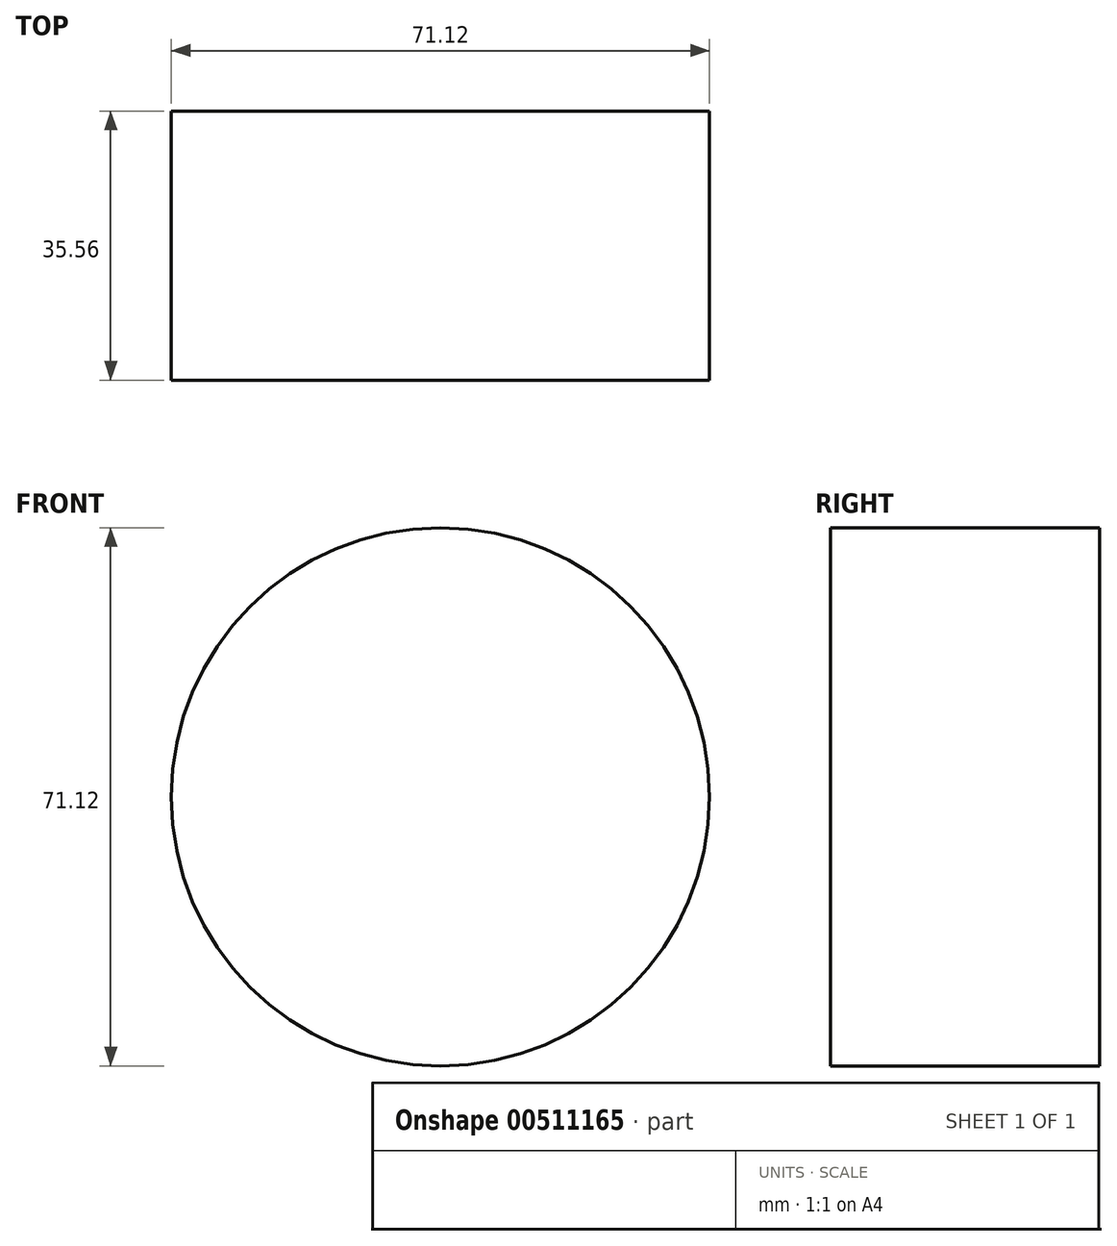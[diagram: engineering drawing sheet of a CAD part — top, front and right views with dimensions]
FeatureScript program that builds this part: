
annotation { "Feature Type Name" : "Feature", "Feature Type Description" : "" }
export const myFeature = defineFeature(function(context is Context, id is Id, definition is map)
    precondition{}
    {
        {
            var Q0;
            Q0=qCreatedBy(makeId("Top.planeOp"),FACE);
            var sketch = newSketch(context, id + "F0", { "sketchPlane" : qUnion([Q0])});
            skLineSegment(sketch, "E0", {"start": v(-19.24, 19.1) * mm, "end": v(-19.24, -16.47) * mm});
            skLineSegment(sketch, "E1", {"start": v(-19.24, -16.47) * mm, "end": v(16.32, -16.47) * mm});
            skLineSegment(sketch, "E2", {"start": v(16.32, -16.47) * mm, "end": v(16.32, 19.1) * mm});
            skLineSegment(sketch, "E3", {"start": v(17.2, 19.1) * mm, "end": v(-19.24, 19.1) * mm});
            skSolve(sketch);
        }
        {
            var Q0;
            {var subQ0=sQuery(id+"F0.wireOp",EDGE,"E0");Q0=makeQuery(id+"F0.imprint","IMPRINT",FACE,{"disambiguationData":[TD([[makeQuery(id+"F0.imprint","IMPRINT",EDGE,{"derivedFrom":subQ0}),1.0]])]});}
            var Q1;
            Q1=sQuery(id+"F0.wireOp",EDGE,"E2");
            revolve(context, id + "F1", {"entities" : qUnion([Q0]), "axis" : qUnion([Q1]), "revolveType" : RevolveType.FULL});
        }
    });
